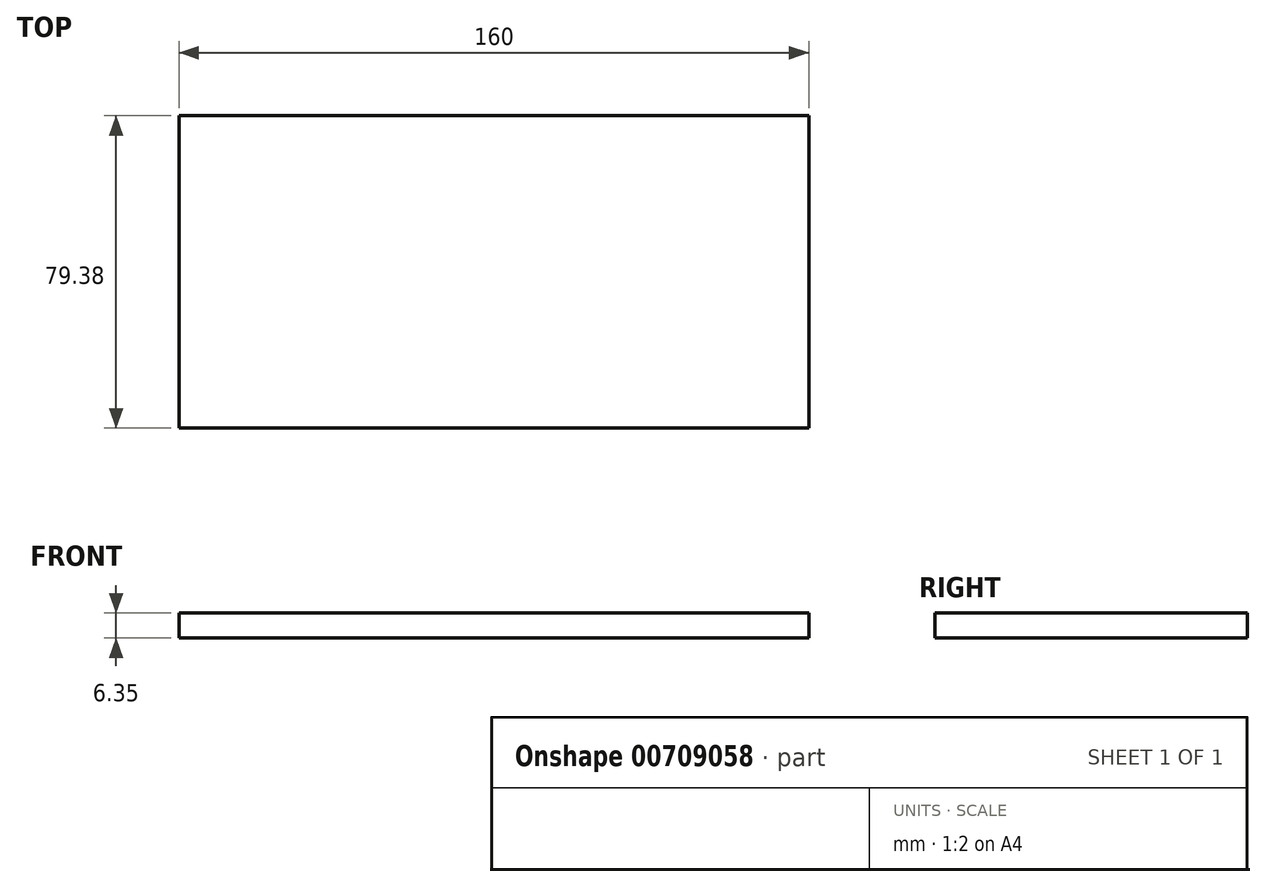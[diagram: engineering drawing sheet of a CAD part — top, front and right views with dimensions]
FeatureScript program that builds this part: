
annotation { "Feature Type Name" : "Feature", "Feature Type Description" : "" }
export const myFeature = defineFeature(function(context is Context, id is Id, definition is map)
    precondition{}
    {
        {
            var Q0;
            Q0=qCreatedBy(makeId("Top.planeOp"),FACE);
            var sketch = newSketch(context, id + "F0", { "sketchPlane" : qUnion([Q0])});
            skLineSegment(sketch, "E0.bottom", {"start": v(0, 0) * mm, "end": v(160, 0) * mm});
            skLineSegment(sketch, "E0.top", {"start": v(0, -79.38) * mm, "end": v(160, -79.38) * mm});
            skLineSegment(sketch, "E0.left", {"start": v(0, 0) * mm, "end": v(0, -79.38) * mm});
            skLineSegment(sketch, "E0.right", {"start": v(160, 0) * mm, "end": v(160, -79.38) * mm});
            skSolve(sketch);
        }
        {
            var Q0;
            Q0=makeQuery(id+"F0.imprint","IMPRINT",FACE,{"disambiguationData":[TD([[makeQuery(id+"F0.imprint","IMPRINT",EDGE,{"derivedFrom":sQuery(id+"F0.wireOp",EDGE,"E0.bottom")}),-1.0]])]});
            extrude(context, id + "F1", {"entities" : qUnion([Q0]), "depth" : 6.35 * mm, "offsetDistance" : 25.4 * mm});
        }
    });
